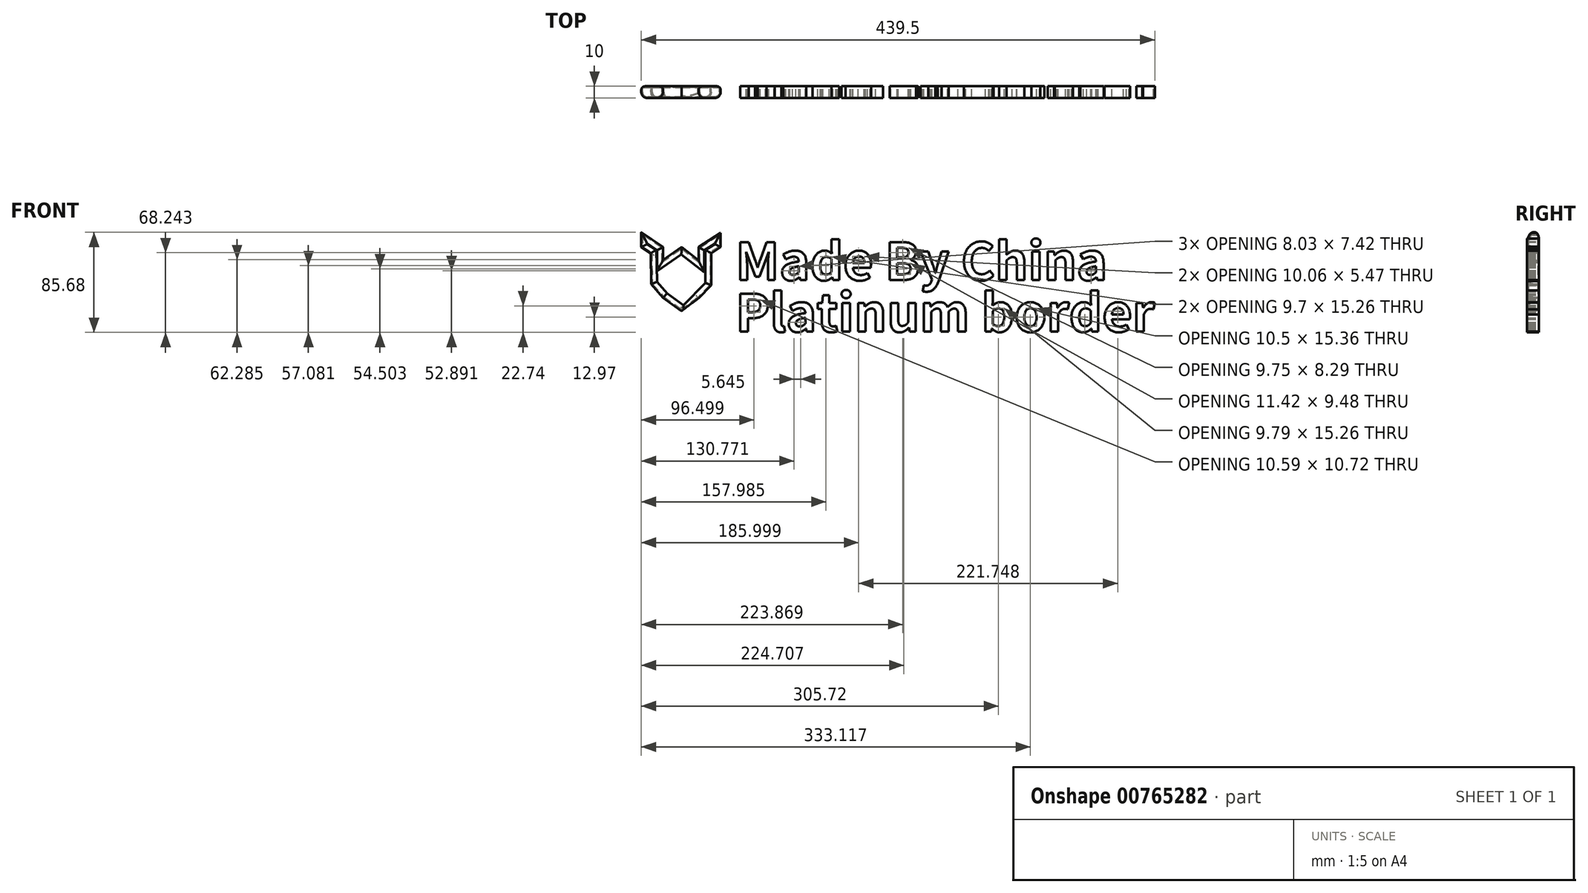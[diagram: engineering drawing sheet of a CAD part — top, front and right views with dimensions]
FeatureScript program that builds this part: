
annotation { "Feature Type Name" : "Feature", "Feature Type Description" : "" }
export const myFeature = defineFeature(function(context is Context, id is Id, definition is map)
    precondition{}
    {
        {
            var Q0;
            Q0=qCreatedBy(makeId("Front.planeOp"),FACE);
            var sketch = newSketch(context, id + "F0", { "sketchPlane" : qUnion([Q0])});
            skLineSegment(sketch, "E0", {"start": v(-15.86, 17.25) * mm, "end": v(-15.86, -15.12) * mm});
            skLineSegment(sketch, "E1", {"start": v(14.5, 16.95) * mm, "end": v(14.5, -15.42) * mm});
            skLineSegment(sketch, "E2", {"start": v(14.5, -15.42) * mm, "end": v(0, -26.42) * mm});
            skLineSegment(sketch, "E3", {"start": v(0, -26.42) * mm, "end": v(-15.86, -15.12) * mm});
            skLineSegment(sketch, "E4", {"start": v(-15.86, 17.25) * mm, "end": v(0, 28.25) * mm});
            skLineSegment(sketch, "E5", {"start": v(0, 28.25) * mm, "end": v(14.5, 16.95) * mm});
            skLineSegment(sketch, "E6", {"start": v(14.5, 16.95) * mm, "end": v(14.5, 28.25) * mm});
            skLineSegment(sketch, "E7", {"start": v(14.5, 28.25) * mm, "end": v(33.44, 40.46) * mm});
            skLineSegment(sketch, "E8", {"start": v(33.44, 40.46) * mm, "end": v(33.44, 28.25) * mm});
            skLineSegment(sketch, "E9", {"start": v(33.44, 28.25) * mm, "end": v(25.44, 23.08) * mm});
            skLineSegment(sketch, "E10", {"start": v(25.44, 23.08) * mm, "end": v(25.44, -4.4) * mm});
            skLineSegment(sketch, "E11", {"start": v(25.44, -4.4) * mm, "end": v(14.5, -15.42) * mm});
            skLineSegment(sketch, "E12", {"start": v(-15.86, 17.25) * mm, "end": v(-15.86, 28.25) * mm});
            skLineSegment(sketch, "E13", {"start": v(-15.86, 28.25) * mm, "end": v(-34.47, 40.95) * mm});
            skLineSegment(sketch, "E14", {"start": v(-34.47, 40.95) * mm, "end": v(-34.47, 28.25) * mm});
            skLineSegment(sketch, "E15", {"start": v(-34.47, 28.25) * mm, "end": v(-26.46, 23.1) * mm});
            skLineSegment(sketch, "E16", {"start": v(-26, -3.37) * mm, "end": v(-15.86, -15.12) * mm});
            skLineSegment(sketch, "E17", {"start": v(-26.46, 23.1) * mm, "end": v(-26, -3.37) * mm});
            skLineSegment(sketch, "E18", {"start": v(11.53, -17.68) * mm, "end": v(11.53, 19.27) * mm});
            skLineSegment(sketch, "E19", {"start": v(-12.68, -17.38) * mm, "end": v(-12.68, 19.46) * mm});
            skLineSegment(sketch, "E20", {"start": v(-15.86, 17.25) * mm, "end": v(-12.68, 19.46) * mm});
            skLineSegment(sketch, "E21", {"start": v(-12.68, -17.38) * mm, "end": v(-15.86, -15.12) * mm});
            skLineSegment(sketch, "E22", {"start": v(11.53, -17.68) * mm, "end": v(14.5, -15.42) * mm});
            skText(sketch, "E23", { "text": "Made By China\nPlatinum border", "fontName": "NotoSansCJKtc-Bold.otf"});
            const initialGuessF0  = {"E23": [0.04619, 0, 1, 0, 0.03176]};
            skSetInitialGuess(sketch, initialGuessF0);
            skSolve(sketch);
        }
        {
            var Q0;
            Q0 = qSketchRegion(id + "F0", true);
            extrude(context, id + "F1", {"entities" : qUnion([Q0]), "depth" : 10 * mm, "offsetDistance" : 25.4 * mm});
        }
        {
            var Q0;
            Q0=makeQuery(id+"F1.opExtrude","CAP_EDGE",EDGE,{"disambiguationData":[OSD([sQuery(id+"F0.wireOp",EDGE,"E13")])],"isStart":false});
            var Q1;
            Q1=makeQuery(id+"F1.opExtrude","CAP_EDGE",EDGE,{"disambiguationData":[OSD([sQuery(id+"F0.wireOp",EDGE,"E12")])],"isStart":false});
            var Q2;
            Q2=makeQuery(id+"F1.opExtrude","CAP_EDGE",EDGE,{"disambiguationData":[OSD([sQuery(id+"F0.wireOp",EDGE,"E4"),sQuery(id+"F0.wireOp",EDGE,"E20")])],"isStart":false});
            var Q3;
            Q3=makeQuery(id+"F1.opExtrude","CAP_EDGE",EDGE,{"disambiguationData":[OSD([sQuery(id+"F0.wireOp",EDGE,"E5")])],"isStart":false});
            var Q4;
            Q4=makeQuery(id+"F1.opExtrude","CAP_EDGE",EDGE,{"disambiguationData":[OSD([sQuery(id+"F0.wireOp",EDGE,"E7")])],"isStart":false});
            var Q5;
            Q5=makeQuery(id+"F1.opExtrude","CAP_EDGE",EDGE,{"disambiguationData":[OSD([sQuery(id+"F0.wireOp",EDGE,"E6")])],"isStart":false});
            var Q6;
            Q6=makeQuery(id+"F1.opExtrude","CAP_EDGE",EDGE,{"disambiguationData":[OSD([sQuery(id+"F0.wireOp",EDGE,"E9")])],"isStart":false});
            var Q7;
            Q7=makeQuery(id+"F1.opExtrude","CAP_EDGE",EDGE,{"disambiguationData":[OSD([sQuery(id+"F0.wireOp",EDGE,"E8")])],"isStart":false});
            var Q8;
            Q8=makeQuery(id+"F1.opExtrude","CAP_EDGE",EDGE,{"disambiguationData":[OSD([sQuery(id+"F0.wireOp",EDGE,"E10")])],"isStart":false});
            var Q9;
            Q9=makeQuery(id+"F1.opExtrude","CAP_EDGE",EDGE,{"disambiguationData":[OSD([sQuery(id+"F0.wireOp",EDGE,"E11")])],"isStart":false});
            var Q10;
            Q10=makeQuery(id+"F1.opExtrude","CAP_EDGE",EDGE,{"disambiguationData":[OSD([sQuery(id+"F0.wireOp",EDGE,"E3"),sQuery(id+"F0.wireOp",EDGE,"E21")])],"isStart":false});
            var Q11;
            Q11=makeQuery(id+"F1.opExtrude","CAP_EDGE",EDGE,{"disambiguationData":[OSD([sQuery(id+"F0.wireOp",EDGE,"E16")])],"isStart":false});
            var Q12;
            Q12=makeQuery(id+"F1.opExtrude","CAP_EDGE",EDGE,{"disambiguationData":[OSD([sQuery(id+"F0.wireOp",EDGE,"E17")])],"isStart":false});
            var Q13;
            Q13=makeQuery(id+"F1.opExtrude","CAP_EDGE",EDGE,{"disambiguationData":[OSD([sQuery(id+"F0.wireOp",EDGE,"E15")])],"isStart":false});
            var Q14;
            Q14=makeQuery(id+"F1.opExtrude","CAP_EDGE",EDGE,{"disambiguationData":[OSD([sQuery(id+"F0.wireOp",EDGE,"E14")])],"isStart":false});
            fillet(context, id + "F2", {"entities" : qUnion([Q0, Q1, Q2, Q3, Q4, Q5, Q6, Q7, Q8, Q9, Q10, Q11, Q12, Q13, Q14]), "radius" : 5 * mm, "tangentPropagation" : true, "allowEdgeOverflow" : false});
        }
        {
            var Q0;
            Q0=makeQuery(id+"F1.opExtrude","CAP_FACE",FACE,{"disambiguationData":[OSD([sQuery(id+"F0.wireOp",EDGE,"E2"),sQuery(id+"F0.wireOp",EDGE,"E3"),sQuery(id+"F0.wireOp",EDGE,"E4"),sQuery(id+"F0.wireOp",EDGE,"E5"),sQuery(id+"F0.wireOp",EDGE,"E6"),sQuery(id+"F0.wireOp",EDGE,"E7"),sQuery(id+"F0.wireOp",EDGE,"E8"),sQuery(id+"F0.wireOp",EDGE,"E9"),sQuery(id+"F0.wireOp",EDGE,"E10"),sQuery(id+"F0.wireOp",EDGE,"E11"),sQuery(id+"F0.wireOp",EDGE,"E12"),sQuery(id+"F0.wireOp",EDGE,"E13"),sQuery(id+"F0.wireOp",EDGE,"E14"),sQuery(id+"F0.wireOp",EDGE,"E15"),sQuery(id+"F0.wireOp",EDGE,"E16"),sQuery(id+"F0.wireOp",EDGE,"E17"),sQuery(id+"F0.wireOp",EDGE,"E20"),sQuery(id+"F0.wireOp",EDGE,"E21"),sQuery(id+"F0.wireOp",EDGE,"E22")])],"isStart":false});
            shell(context, id + "F3", {"entities" : qUnion([Q0]), "thickness" : 1 * mm});
        }
        {
            var Q0;
            Q0=makeQuery(id+"F1.opExtrude","CAP_EDGE",EDGE,{"disambiguationData":[OSD([sQuery(id+"F0.wireOp",EDGE,"E5")])],"isStart":true});
            var Q1;
            Q1=makeQuery(id+"F1.opExtrude","CAP_EDGE",EDGE,{"disambiguationData":[OSD([sQuery(id+"F0.wireOp",EDGE,"E13")])],"isStart":true});
            var Q2;
            Q2=makeQuery(id+"F1.opExtrude","CAP_EDGE",EDGE,{"disambiguationData":[OSD([sQuery(id+"F0.wireOp",EDGE,"E4"),sQuery(id+"F0.wireOp",EDGE,"E20")])],"isStart":true});
            var Q3;
            Q3=makeQuery(id+"F1.opExtrude","CAP_EDGE",EDGE,{"disambiguationData":[OSD([sQuery(id+"F0.wireOp",EDGE,"E12")])],"isStart":true});
            var Q4;
            Q4=makeQuery(id+"F1.opExtrude","CAP_EDGE",EDGE,{"disambiguationData":[OSD([sQuery(id+"F0.wireOp",EDGE,"E17")])],"isStart":true});
            var Q5;
            Q5=makeQuery(id+"F1.opExtrude","CAP_EDGE",EDGE,{"disambiguationData":[OSD([sQuery(id+"F0.wireOp",EDGE,"E14")])],"isStart":true});
            var Q6;
            Q6=makeQuery(id+"F1.opExtrude","CAP_EDGE",EDGE,{"disambiguationData":[OSD([sQuery(id+"F0.wireOp",EDGE,"E16")])],"isStart":true});
            var Q7;
            Q7=makeQuery(id+"F1.opExtrude","CAP_EDGE",EDGE,{"disambiguationData":[OSD([sQuery(id+"F0.wireOp",EDGE,"E3"),sQuery(id+"F0.wireOp",EDGE,"E21")])],"isStart":true});
            var Q8;
            Q8=makeQuery(id+"F1.opExtrude","CAP_EDGE",EDGE,{"disambiguationData":[OSD([sQuery(id+"F0.wireOp",EDGE,"E2"),sQuery(id+"F0.wireOp",EDGE,"E22")])],"isStart":true});
            var Q9;
            Q9=makeQuery(id+"F1.opExtrude","CAP_EDGE",EDGE,{"disambiguationData":[OSD([sQuery(id+"F0.wireOp",EDGE,"E11")])],"isStart":true});
            var Q10;
            Q10=makeQuery(id+"F1.opExtrude","CAP_EDGE",EDGE,{"disambiguationData":[OSD([sQuery(id+"F0.wireOp",EDGE,"E10")])],"isStart":true});
            var Q11;
            Q11=makeQuery(id+"F1.opExtrude","CAP_EDGE",EDGE,{"disambiguationData":[OSD([sQuery(id+"F0.wireOp",EDGE,"E9")])],"isStart":true});
            var Q12;
            Q12=makeQuery(id+"F1.opExtrude","CAP_EDGE",EDGE,{"disambiguationData":[OSD([sQuery(id+"F0.wireOp",EDGE,"E8")])],"isStart":true});
            var Q13;
            Q13=makeQuery(id+"F1.opExtrude","CAP_EDGE",EDGE,{"disambiguationData":[OSD([sQuery(id+"F0.wireOp",EDGE,"E7")])],"isStart":true});
            var Q14;
            Q14=makeQuery(id+"F1.opExtrude","CAP_EDGE",EDGE,{"disambiguationData":[OSD([sQuery(id+"F0.wireOp",EDGE,"E6")])],"isStart":true});
            fillet(context, id + "F4", {"entities" : qUnion([Q0, Q1, Q2, Q3, Q4, Q5, Q6, Q7, Q8, Q9, Q10, Q11, Q12, Q13, Q14]), "radius" : 3 * mm, "tangentPropagation" : true, "allowEdgeOverflow" : false});
        }
    });
